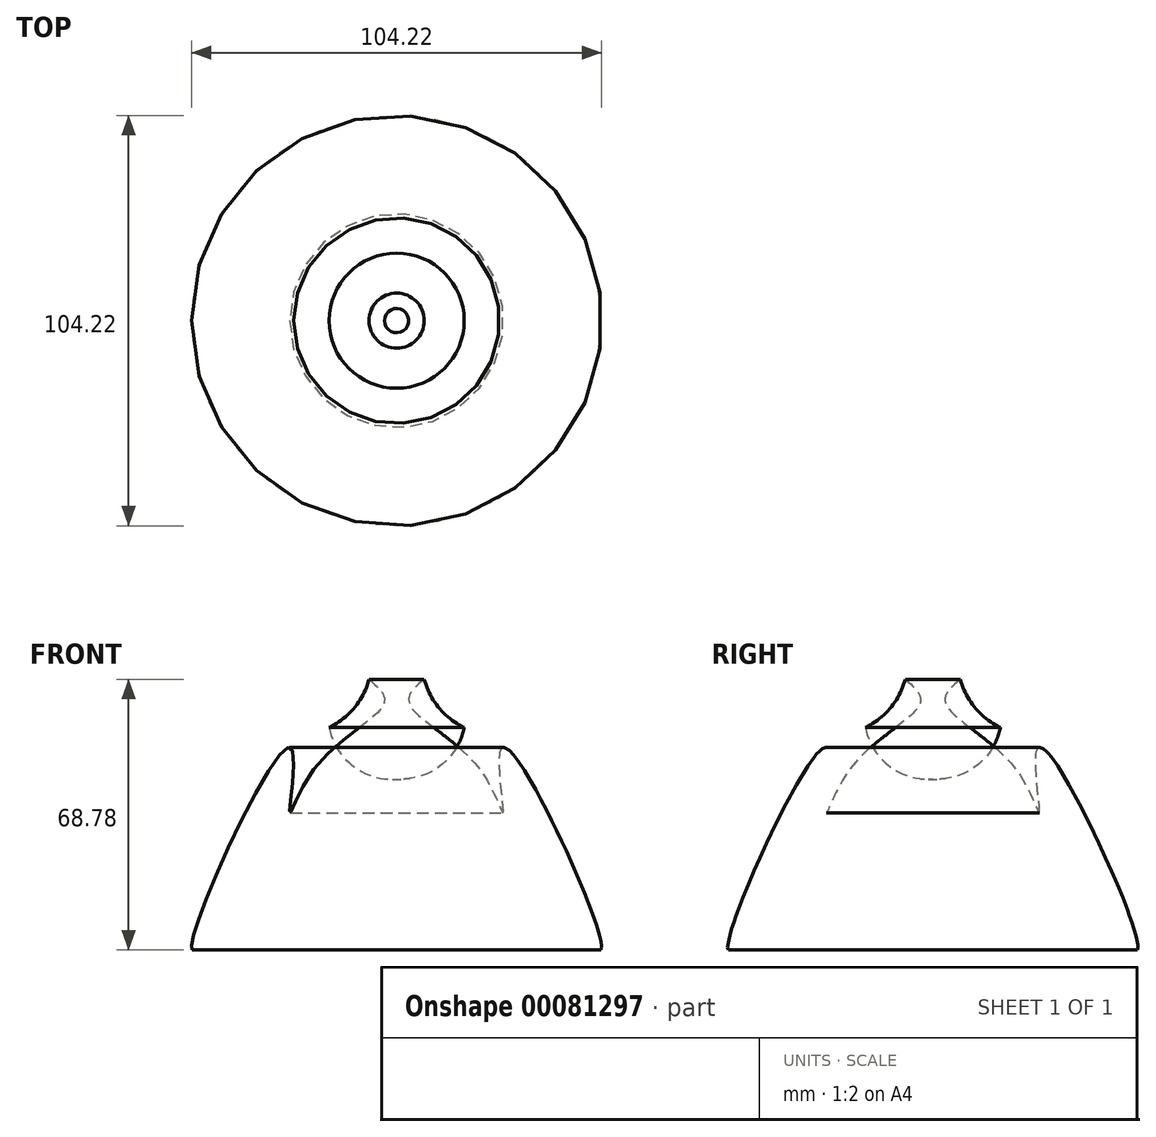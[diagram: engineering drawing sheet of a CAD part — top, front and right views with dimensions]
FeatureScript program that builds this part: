
annotation { "Feature Type Name" : "Feature", "Feature Type Description" : "" }
export const myFeature = defineFeature(function(context is Context, id is Id, definition is map)
    precondition{}
    {
        {
            var Q0;
            Q0=qCreatedBy(makeId("Front.planeOp"),FACE);
            var sketch = newSketch(context, id + "F0", { "sketchPlane" : qUnion([Q0])});
            skArc(sketch, "E0", {"start": v(17.17, 56.48) * mm, "mid": v(13.47, 70.6) * mm, "end": v(0, 76.2) * mm});
            skArc(sketch, "E1", {"start": v(7, 68.78) * mm, "mid": v(10.75, 61.53) * mm, "end": v(17.17, 56.48) * mm});
            skFitSpline(sketch, "E2", {"points": [v(7, 68.78) * mm, v(3.18, 62.84) * mm, v(20.77, 46.31) * mm, v(27.13, 35.08) * mm, v(26.7, 51.19) * mm, v(47.05, 16.21) * mm, v(51.93, 0) * mm, v(51.3, 0) * mm], "startDerivative": vector(-65.62, -56.5) * mm, "endDerivative": vector(-24.14, 6.6) * mm});
            skLineSegment(sketch, "E3", {"start": v(51.93, 0) * mm, "end": v(0, 0) * mm});
            skLineSegment(sketch, "E4", {"start": v(0, 0) * mm, "end": v(0, 76.2) * mm});
            skSolve(sketch);
        }
        {
            var Q0;
            Q0=makeQuery(id+"F0.imprint","IMPRINT",FACE,{"disambiguationData":[TD([[makeQuery(id+"F0.imprint","IMPRINT",EDGE,{"derivedFrom":sQuery(id+"F0.wireOp",EDGE,"E0")}),1.0]])]});
            var Q1;
            Q1=sQuery(id+"F0.wireOp",EDGE,"E4");
            revolve(context, id + "F1", {"entities" : qUnion([Q0]), "axis" : qUnion([Q1]), "revolveType" : RevolveType.FULL});
        }
    });
